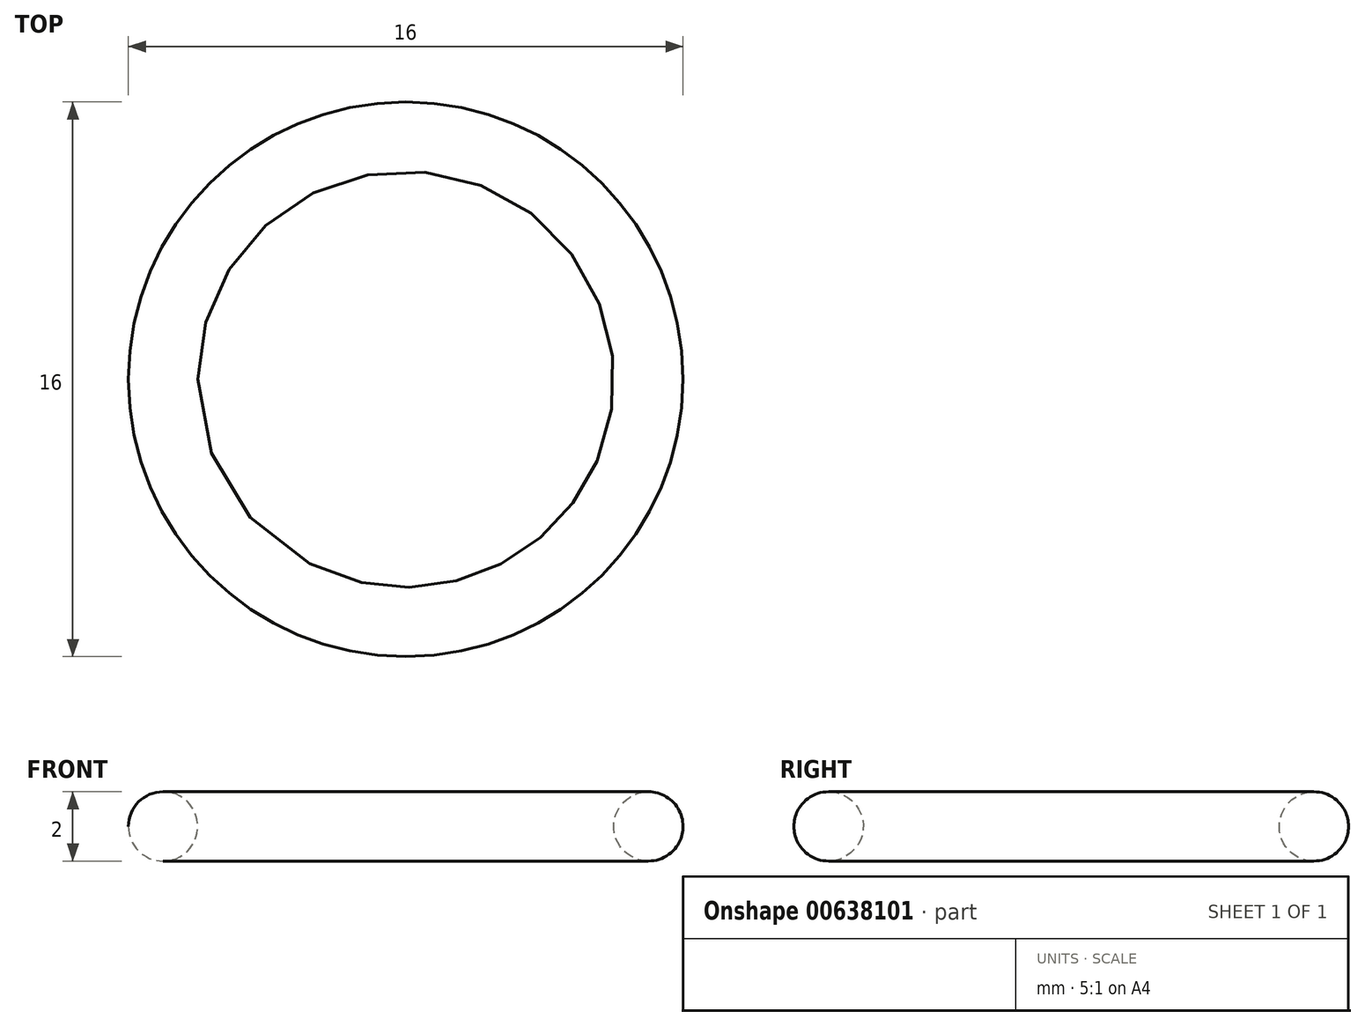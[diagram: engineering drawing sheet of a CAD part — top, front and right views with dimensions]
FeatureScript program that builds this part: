
annotation { "Feature Type Name" : "Feature", "Feature Type Description" : "" }
export const myFeature = defineFeature(function(context is Context, id is Id, definition is map)
    precondition{}
    {
        {
            var Q0;
            Q0=qCreatedBy(makeId("Front.planeOp"),FACE);
            var sketch = newSketch(context, id + "F0", { "sketchPlane" : qUnion([Q0])});
            skCircle(sketch, "E0", {"center": v(7, 0) * mm, "radius": 1 * mm});
            skLineSegment(sketch, "E1", {"start": v(0, 0) * mm, "end": v(0, 10) * mm, "construction": true});
            skSolve(sketch);
        }
        {
            var Q0;
            Q0=makeQuery(id+"F0.imprint","IMPRINT",FACE,{"disambiguationData":[TD([[makeQuery(id+"F0.imprint","IMPRINT",EDGE,{"derivedFrom":sQuery(id+"F0.wireOp",EDGE,"E0")}),1.0]])]});
            var Q1;
            Q1=sQuery(id+"F0.wireOp",EDGE,"E1");
            revolve(context, id + "F1", {"entities" : qUnion([Q0]), "axis" : qUnion([Q1]), "revolveType" : RevolveType.FULL});
        }
    });
